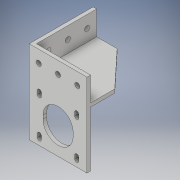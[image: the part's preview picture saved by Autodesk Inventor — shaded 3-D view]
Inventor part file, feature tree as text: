
AUTODESK INVENTOR PART (.ipt)
format: ipt  version: 2018 (Build 220112000, 112)  size: 222,208 bytes
history: native  units: in
note: dims shown in document units (in); Inventor stores cm internally (conversion verified against a paired STEP export)
features: extrude x8, sketch x8, projected_geometry x1
ambient origin geometry x8: Origin, YZ Plane, XZ Plane, XY Plane, X Axis, Y Axis, Z Axis, Center Point
bodies: Solid1 (feature_tree)
feature tree (17):
  extrude  "Extrusion1"  Depth=0.9055in
  extrude  "Extrusion2"  Depth=0.1181in TaperAngle=0.0deg
  sketch  "Sketch3"  dims[d6=1.8898in d7=1.811in]
  extrude  "Extrusion4"  Depth=1.811in
  extrude  "Extrusion8"  Depth=0.1181in
  extrude  "Extrusion9"  Depth=0.3346in
  extrude  "Extrusion10"  Depth=1.2205in
  extrude  "Extrusion11"  Depth=0.1181in TaperAngle=0.0deg
  extrude  "Extrusion12"  Depth=0.3937in
  sketch  "Sketch1"  dims[d0=0.9055in d1=0.9055in]
  sketch  "Sketch2"  dims[d2=1.8898in d4=0.1181in d5=0.0in]
  sketch  "Sketch4"  dims[d8=0.126in d9=0.1181in]
  projected_geometry  "Projected Loop1"
  sketch  "Sketch8"  dims[d10=0.3346in d11=0.1969in]
  sketch  "Sketch9"  dims[d12=1.2205in d13=1.2205in]
  sketch  "Sketch10"  dims[d14=0.1181in d15=0.2362in d16=0.0in]
  sketch  "Sketch11"  dims[d19=0.1654in d20=0.6299in d21=0.315in d23=0.6299in d30=0.1181in d31=1.9685in d32=0.0in d46=0.9843in d47=0.1181in d48=0.1181in d49=0.0in d50=0.1181in d51=0.0in d52=0.3937in d53=0.1181in d54=0.0in d55=0.7874in d56=0.7874in d57=0.1181in d58=0.0in d59=0.1654in d60=0.6299in d61=0.5118in d62=0.6299in d63=0.1181in d64=0.0in d65=0.3937in]
